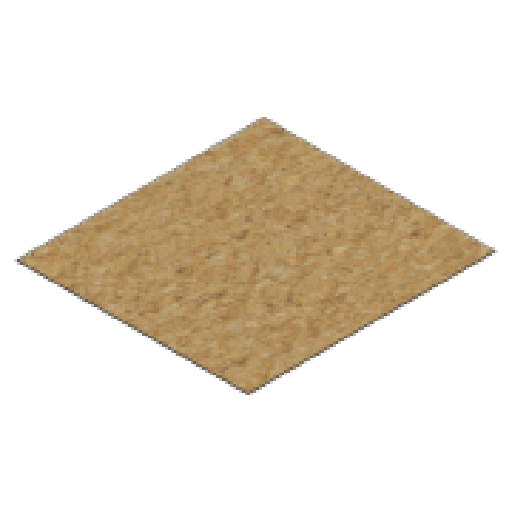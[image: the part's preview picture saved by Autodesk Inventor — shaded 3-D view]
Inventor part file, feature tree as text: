
AUTODESK INVENTOR PART (.ipt)
format: ipt  version: 2024 (Build 280153000, 153)  size: 109,568 bytes
history: native  units: in
note: dims shown in document units (in); Inventor stores cm internally (conversion verified against a paired STEP export)
features: extrude x1, sketch x1
ambient origin geometry x8: Origin, YZ Plane, XZ Plane, XY Plane, X Axis, Y Axis, Z Axis, Center Point
bodies: Solid1 (feature_tree)
feature tree (2):
  extrude  "Extrusion1"  Depth=23.622in
  sketch  "Sketch1"  dims[d0=22.126in d1=23.622in d2=0.1181in d3=0.0in]
